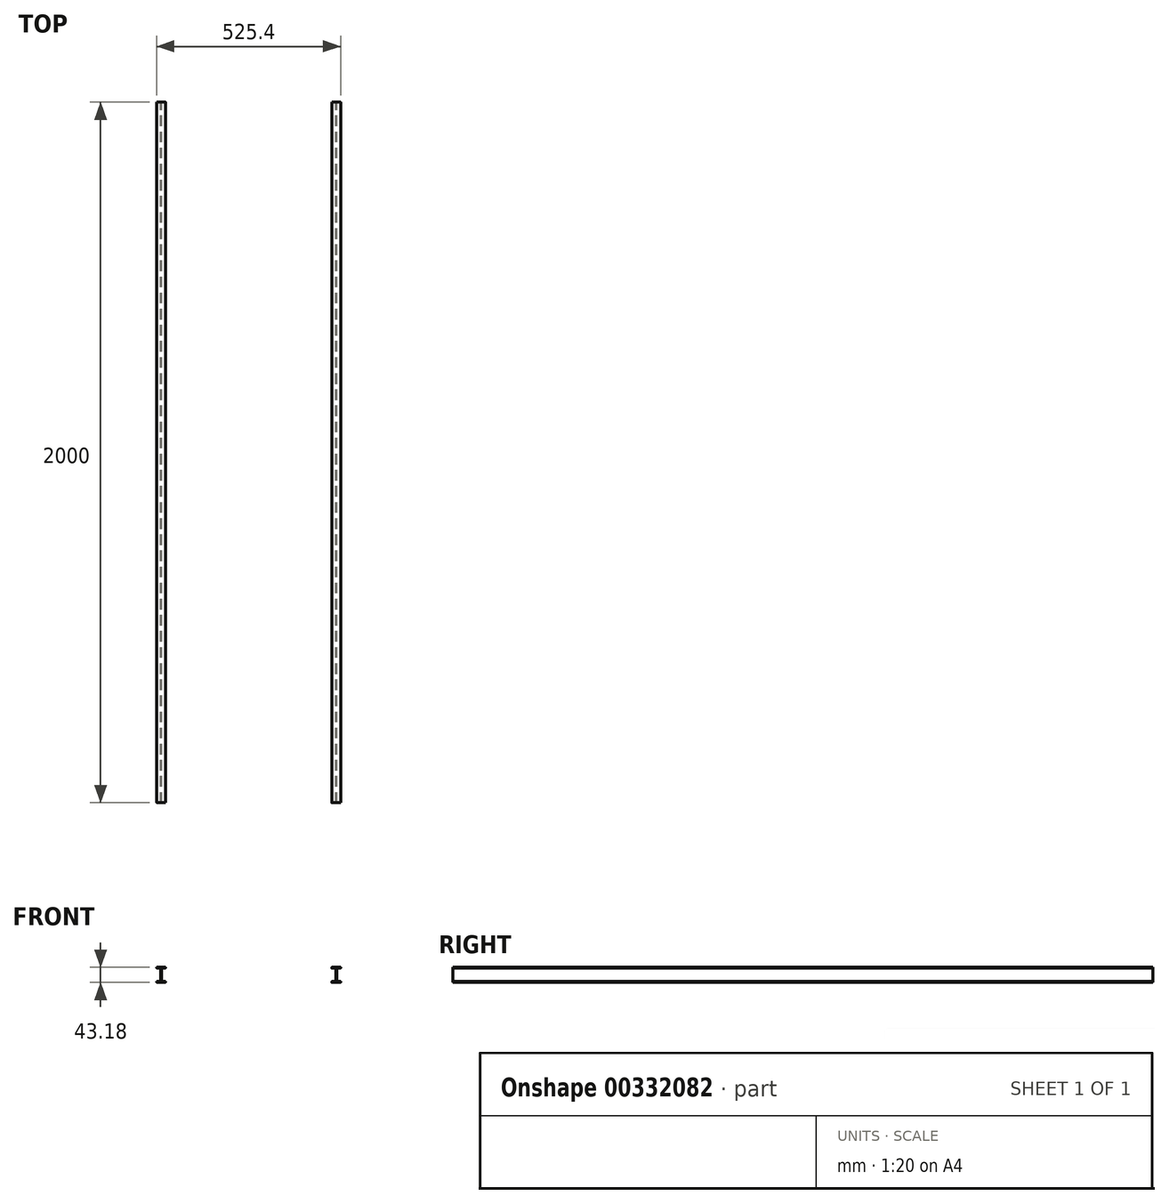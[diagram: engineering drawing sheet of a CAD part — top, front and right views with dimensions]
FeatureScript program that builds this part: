
annotation { "Feature Type Name" : "Feature", "Feature Type Description" : "" }
export const myFeature = defineFeature(function(context is Context, id is Id, definition is map)
    precondition{}
    {
        {
            var Q0;
            Q0=qCreatedBy(makeId("Front.planeOp"),FACE);
            var sketch = newSketch(context, id + "F0", { "sketchPlane" : qUnion([Q0])});
            skLineSegment(sketch, "E0", {"start": v(0, 19.05) * mm, "end": v(0, -19.05) * mm, "construction": true});
            skLineSegment(sketch, "E1", {"start": v(-12.45, 19.05) * mm, "end": v(-2.54, 19.05) * mm});
            skLineSegment(sketch, "E2", {"start": v(-12.45, -19.05) * mm, "end": v(-2.54, -19.05) * mm});
            skLineSegment(sketch, "E3.0", {"start": v(-12.45, -21.59) * mm, "end": v(12.45, -21.59) * mm});
            skLineSegment(sketch, "E4.0", {"start": v(-12.45, 21.6) * mm, "end": v(12.45, 21.6) * mm});
            skLineSegment(sketch, "E5.0", {"start": v(-1.27, 17.78) * mm, "end": v(-1.27, -17.78) * mm});
            skLineSegment(sketch, "E6.0", {"start": v(1.27, 17.78) * mm, "end": v(1.27, -17.78) * mm});
            skLineSegment(sketch, "E7", {"start": v(-12.7, -21.34) * mm, "end": v(-12.7, -19.3) * mm});
            skLineSegment(sketch, "E8", {"start": v(12.7, -19.3) * mm, "end": v(12.7, -21.34) * mm});
            skLineSegment(sketch, "E9", {"start": v(12.7, 19.3) * mm, "end": v(12.7, 21.34) * mm});
            skLineSegment(sketch, "E10", {"start": v(-12.7, 21.34) * mm, "end": v(-12.7, 19.3) * mm});
            skLineSegment(sketch, "E11.trimOffspring", {"start": v(2.54, 19.05) * mm, "end": v(12.45, 19.05) * mm});
            skLineSegment(sketch, "E12.trimOffspring", {"start": v(2.54, -19.05) * mm, "end": v(12.45, -19.05) * mm});
            skPoint(sketch, "E13.visualSharp", {"position": v(-1.27, 19.05) * mm});
            skArc(sketch, "E13.filletArc", {"start": v(-1.27, 17.78) * mm, "mid": v(-1.64, 18.68) * mm, "end": v(-2.54, 19.05) * mm});
            skPoint(sketch, "E14.visualSharp", {"position": v(1.27, 19.05) * mm});
            skArc(sketch, "E14.filletArc", {"start": v(2.54, 19.05) * mm, "mid": v(1.64, 18.68) * mm, "end": v(1.27, 17.78) * mm});
            skPoint(sketch, "E15.visualSharp", {"position": v(-1.27, -19.05) * mm});
            skArc(sketch, "E15.filletArc", {"start": v(-2.54, -19.05) * mm, "mid": v(-1.64, -18.68) * mm, "end": v(-1.27, -17.78) * mm});
            skPoint(sketch, "E16.visualSharp", {"position": v(1.27, -19.05) * mm});
            skArc(sketch, "E16.filletArc", {"start": v(1.27, -17.78) * mm, "mid": v(1.64, -18.68) * mm, "end": v(2.54, -19.05) * mm});
            skPoint(sketch, "E17.visualSharp", {"position": v(-12.7, -19.05) * mm});
            skArc(sketch, "E17.filletArc", {"start": v(-12.45, -19.05) * mm, "mid": v(-12.63, -19.12) * mm, "end": v(-12.7, -19.3) * mm});
            skPoint(sketch, "E18.visualSharp", {"position": v(-12.7, -21.59) * mm});
            skArc(sketch, "E18.filletArc", {"start": v(-12.7, -21.34) * mm, "mid": v(-12.63, -21.52) * mm, "end": v(-12.45, -21.59) * mm});
            skPoint(sketch, "E19.visualSharp", {"position": v(12.7, -21.59) * mm});
            skArc(sketch, "E19.filletArc", {"start": v(12.45, -21.59) * mm, "mid": v(12.63, -21.52) * mm, "end": v(12.7, -21.34) * mm});
            skPoint(sketch, "E20.visualSharp", {"position": v(12.7, -19.05) * mm});
            skArc(sketch, "E20.filletArc", {"start": v(12.7, -19.3) * mm, "mid": v(12.63, -19.12) * mm, "end": v(12.45, -19.05) * mm});
            skPoint(sketch, "E21.visualSharp", {"position": v(12.7, 19.05) * mm});
            skArc(sketch, "E21.filletArc", {"start": v(12.45, 19.05) * mm, "mid": v(12.63, 19.12) * mm, "end": v(12.7, 19.3) * mm});
            skPoint(sketch, "E22.visualSharp", {"position": v(12.7, 21.6) * mm});
            skArc(sketch, "E22.filletArc", {"start": v(12.7, 21.34) * mm, "mid": v(12.63, 21.52) * mm, "end": v(12.45, 21.6) * mm});
            skPoint(sketch, "E23.visualSharp", {"position": v(-12.7, 21.6) * mm});
            skArc(sketch, "E23.filletArc", {"start": v(-12.45, 21.6) * mm, "mid": v(-12.63, 21.52) * mm, "end": v(-12.7, 21.34) * mm});
            skPoint(sketch, "E24.visualSharp", {"position": v(-12.7, 19.05) * mm});
            skArc(sketch, "E24.filletArc", {"start": v(-12.7, 19.3) * mm, "mid": v(-12.63, 19.12) * mm, "end": v(-12.45, 19.05) * mm});
            skSolve(sketch);
        }
        {
            var Q0;
            Q0=makeQuery(id+"F0.imprint","IMPRINT",FACE,{"disambiguationData":[TD([[makeQuery(id+"F0.imprint","IMPRINT",EDGE,{"derivedFrom":sQuery(id+"F0.wireOp",EDGE,"E1")}),1.0]])]});
            extrude(context, id + "F1", {"entities" : qUnion([Q0]), "depth" : 2000 * mm});
        }
        {
            var Q0;
            Q0=makeQuery(id+"F1.opExtrude","SWEPT_BODY",BODY,{"disambiguationData":[OSD([sQuery(id+"F0.wireOp",EDGE,"E1"),sQuery(id+"F0.wireOp",EDGE,"E2"),sQuery(id+"F0.wireOp",EDGE,"E3.0"),sQuery(id+"F0.wireOp",EDGE,"E4.0"),sQuery(id+"F0.wireOp",EDGE,"E5.0"),sQuery(id+"F0.wireOp",EDGE,"E6.0"),sQuery(id+"F0.wireOp",EDGE,"E7"),sQuery(id+"F0.wireOp",EDGE,"E8"),sQuery(id+"F0.wireOp",EDGE,"E9"),sQuery(id+"F0.wireOp",EDGE,"E10"),sQuery(id+"F0.wireOp",EDGE,"E11.trimOffspring"),sQuery(id+"F0.wireOp",EDGE,"E12.trimOffspring"),sQuery(id+"F0.wireOp",EDGE,"E13.filletArc"),sQuery(id+"F0.wireOp",EDGE,"E14.filletArc"),sQuery(id+"F0.wireOp",EDGE,"E15.filletArc"),sQuery(id+"F0.wireOp",EDGE,"E16.filletArc"),sQuery(id+"F0.wireOp",EDGE,"E17.filletArc"),sQuery(id+"F0.wireOp",EDGE,"E18.filletArc"),sQuery(id+"F0.wireOp",EDGE,"E19.filletArc"),sQuery(id+"F0.wireOp",EDGE,"E20.filletArc"),sQuery(id+"F0.wireOp",EDGE,"E21.filletArc"),sQuery(id+"F0.wireOp",EDGE,"E22.filletArc"),sQuery(id+"F0.wireOp",EDGE,"E23.filletArc"),sQuery(id+"F0.wireOp",EDGE,"E24.filletArc")])]});
            transform(context, id + "F2", {"entities" : qUnion([Q0]), "transformType" : TransformType.TRANSLATION_3D, "dx" : 500 * mm, "dy" : 0 * mm, "dz" : 0 * mm, "makeCopy" : true});
        }
    });
